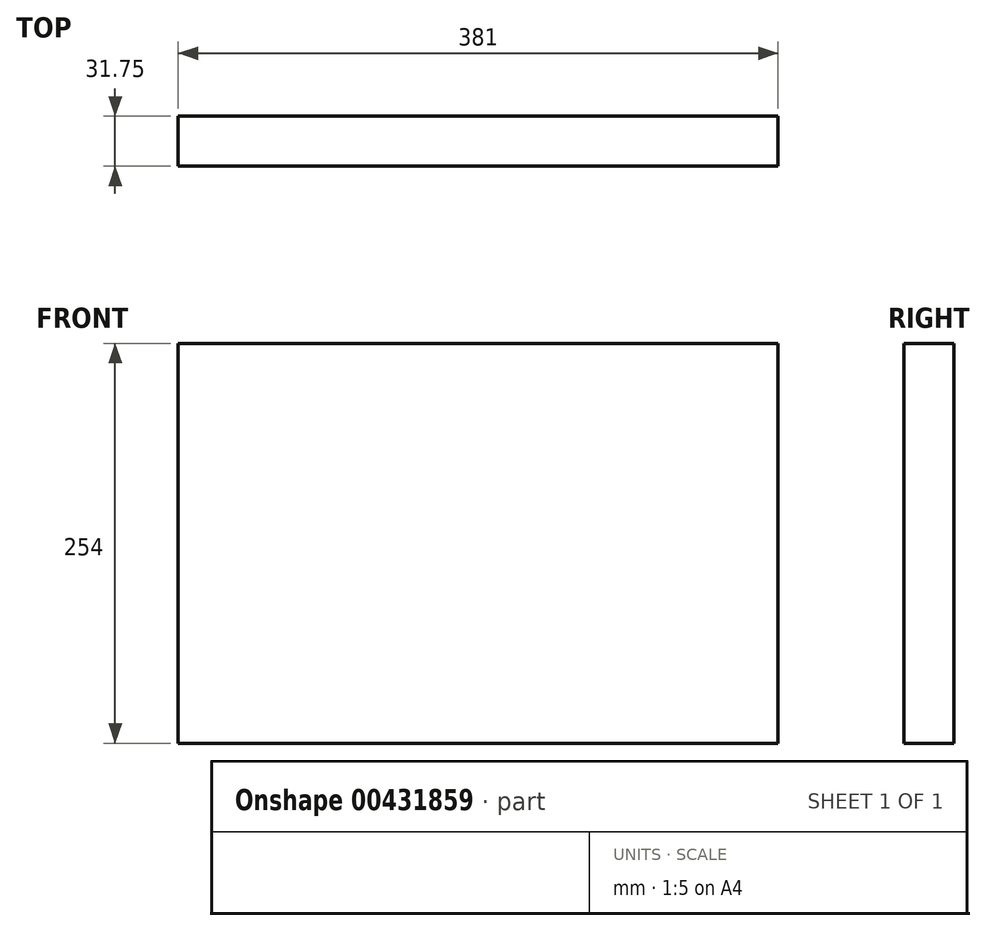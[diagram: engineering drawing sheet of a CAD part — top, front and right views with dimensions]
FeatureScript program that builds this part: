
annotation { "Feature Type Name" : "Feature", "Feature Type Description" : "" }
export const myFeature = defineFeature(function(context is Context, id is Id, definition is map)
    precondition{}
    {
        {
            var Q0;
            Q0=qCreatedBy(makeId("Front.planeOp"),FACE);
            var sketch = newSketch(context, id + "F0", { "sketchPlane" : qUnion([Q0])});
            skLineSegment(sketch, "E0.bottom", {"start": v(0, 0) * mm, "end": v(381, 0) * mm});
            skLineSegment(sketch, "E0.top", {"start": v(0, 254) * mm, "end": v(381, 254) * mm});
            skLineSegment(sketch, "E0.left", {"start": v(0, 0) * mm, "end": v(0, 254) * mm});
            skLineSegment(sketch, "E0.right", {"start": v(381, 0) * mm, "end": v(381, 254) * mm});
            skSolve(sketch);
        }
        {
            var Q0;
            Q0=makeQuery(id+"F0.imprint","IMPRINT",FACE,{"disambiguationData":[TD([[makeQuery(id+"F0.imprint","IMPRINT",EDGE,{"derivedFrom":sQuery(id+"F0.wireOp",EDGE,"E0.bottom")}),1.0]])]});
            extrude(context, id + "F1", {"entities" : qUnion([Q0]), "depth" : 31.75 * mm});
        }
    });
